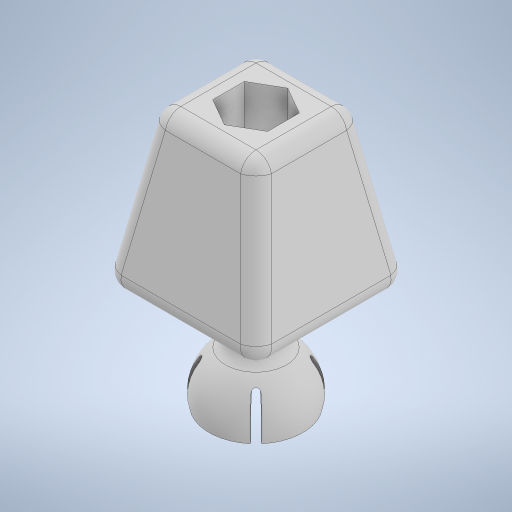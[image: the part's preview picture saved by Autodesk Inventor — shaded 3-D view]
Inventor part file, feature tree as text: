
AUTODESK INVENTOR PART (.ipt)
format: ipt  version: 2023 (Build 270158000, 158)  size: 894,976 bytes
history: native  units: mm
features: sketch x7, fillet x5, chamfer x4, revolve x3, mirror x3, extrude x2, other x1
ambient origin geometry x8: Origin, YZ Plane, XZ Plane, XY Plane, X Axis, Y Axis, Z Axis, Center Point
bodies: Body1 (feature_tree)
feature tree (25):
  other  "Bryła1"
  sketch  "Szkic1"
  extrude  "Wyciągnięcie proste1"  Depth=50.0mm
  chamfer  "Faza1"  Distance=50.0mm
  chamfer  "Faza2"  Distance=50.0mm
  chamfer  "Faza3"  Distance=50.0mm
  chamfer  "Faza4"  Distance=50.0mm
  extrude  "Wyciągnięcie proste2"  Depth=50.0mm
  fillet  "Zaokrąglenie1"  Radius=50.0mm
  revolve  "Obrót1"
  revolve  "Obrót2"
  mirror  "Odbij1"
  mirror  "Odbij2"
  mirror  "Odbij3"
  sketch  "Szkic9"
  revolve  "Obrót3"
  fillet  "Zaokrąglenie5"  Radius=17.5mm
  fillet  "Zaokrąglenie6"  Radius=40.0mm
  fillet  "Zaokrąglenie7"  Radius=5.0mm
  fillet  "Zaokrąglenie8"  Radius=15.0mm
  sketch  "Szkic2"
  sketch  "Szkic3"
  sketch  "Szkic6"
  sketch  "Szkic8"
  sketch  "Szkic10"
